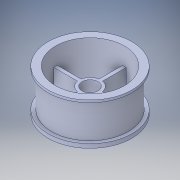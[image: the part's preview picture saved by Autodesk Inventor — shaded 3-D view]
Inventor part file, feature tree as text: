
AUTODESK INVENTOR PART (.ipt)
format: ipt  version: 2016 (Build 200138000, 138)  size: 536,064 bytes
history: native  units: in
note: dims shown in document units (in); Inventor stores cm internally (conversion verified against a paired STEP export)
features: sketch x1, other x1
ambient origin geometry x8: Origin, YZ Plane, XZ Plane, XY Plane, X Axis, Y Axis, Z Axis, Center Point
bodies: Solid1 (feature_tree)
feature tree (2):
  sketch  "Sketch1"
  other  "Cut-Extrude3"
